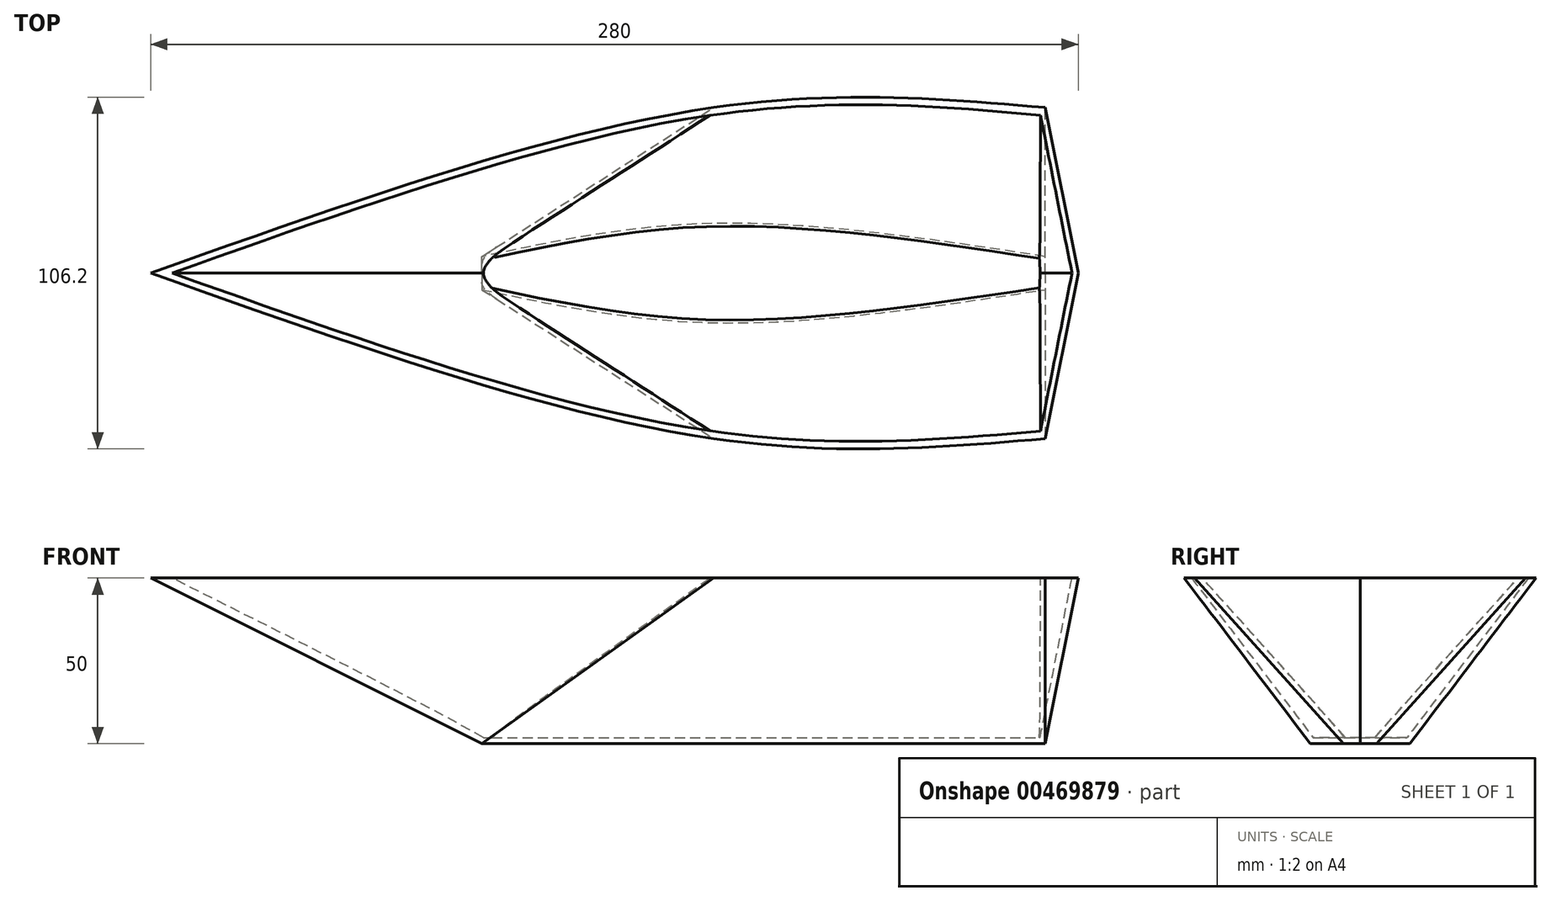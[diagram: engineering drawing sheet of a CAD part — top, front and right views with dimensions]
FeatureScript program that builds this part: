
annotation { "Feature Type Name" : "Feature", "Feature Type Description" : "" }
export const myFeature = defineFeature(function(context is Context, id is Id, definition is map)
    precondition{}
    {
        {
            var Q0;
            Q0=qCreatedBy(makeId("Top.planeOp"),FACE);
            var sketch = newSketch(context, id + "F0", { "sketchPlane" : qUnion([Q0])});
            skLineSegment(sketch, "E0", {"start": v(-100, 50) * mm, "end": v(-270, 50) * mm});
            skLineSegment(sketch, "E1", {"start": v(-100, -50) * mm, "end": v(-270, -50) * mm});
            skLineSegment(sketch, "E2", {"start": v(-270, 50) * mm, "end": v(-270, 0) * mm});
            skLineSegment(sketch, "E3", {"start": v(0, 50) * mm, "end": v(10, 0) * mm});
            skLineSegment(sketch, "E4", {"start": v(10, 0) * mm, "end": v(0, -50) * mm});
            skFitSpline(sketch, "E5", {"points": [v(-270, 0) * mm, v(-100, 50) * mm, v(0, 50) * mm], "startDerivative": vector(316.15, 112.56) * mm, "endDerivative": vector(219.26, -18.78) * mm});
            skFitSpline(sketch, "E6", {"points": [v(0, -50) * mm, v(-100, -50) * mm, v(-270, 0) * mm], "startDerivative": vector(-219.26, -18.78) * mm, "endDerivative": vector(-316.15, 112.56) * mm});
            skSolve(sketch);
        }
        {
            var Q0;
            Q0=qCreatedBy(makeId("Top.planeOp"),FACE);
            cPlane(context, id + "F1", {"entities" : qUnion([Q0]), "cplaneType" : CPlaneType.OFFSET, "offset" : 50 * mm, "oppositeDirection" : true, "width" : 150 * mm, "height" : 150 * mm});
        }
        {
            var Q0;
            Q0=qCreatedBy(id+"F1.planeOp",FACE);
            var sketch = newSketch(context, id + "F2", { "sketchPlane" : qUnion([Q0])});
            skLineSegment(sketch, "E7", {"start": v(0, 0) * mm, "end": v(5, 0) * mm});
            skLineSegment(sketch, "E8", {"start": v(0, 0) * mm, "end": v(0, -5) * mm});
            skLineSegment(sketch, "E9", {"start": v(0, 0) * mm, "end": v(0, 5) * mm});
            skLineSegment(sketch, "E10", {"start": v(-170, 0) * mm, "end": v(-170, -5) * mm});
            skLineSegment(sketch, "E11", {"start": v(-170, 0) * mm, "end": v(-170, 5) * mm});
            skFitSpline(sketch, "E12", {"points": [v(-170, -5) * mm, v(-100, -15) * mm, v(0, -5) * mm], "startDerivative": vector(146.51, -31.12) * mm, "endDerivative": vector(192.15, 29.35) * mm});
            skFitSpline(sketch, "E13", {"points": [v(0, 5) * mm, v(-100, 15) * mm, v(-170, 5) * mm], "startDerivative": vector(-192.15, 29.35) * mm, "endDerivative": vector(-146.51, -31.12) * mm});
            skSolve(sketch);
        }
        {
            var Q0;
            Q0=makeQuery(id+"F2.imprint","IMPRINT",FACE,{"disambiguationData":[TD([[makeQuery(id+"F2.imprint","IMPRINT",EDGE,{"derivedFrom":sQuery(id+"F2.wireOp",EDGE,"E8")}),-1.0]])]});
            var Q1;
            {var subQ2=sQuery(id+"F0.wireOp",EDGE,"E3");Q1=makeQuery(id+"F0.imprint","IMPRINT",FACE,{"disambiguationData":[TD([[makeQuery(id+"F0.imprint","IMPRINT",EDGE,{"derivedFrom":subQ2}),-1.0]])]});}
            loft(context, id + "F3", {"sheetProfilesArray" : [{ "sheetProfileEntities" : qUnion([Q0]) }, { "sheetProfileEntities" : qUnion([Q1]) }]});
        }
        {
            var Q0;
            {var subQ2=sQuery(id+"F0.wireOp",EDGE,"E3");Q0=makeQuery(id+"F3.opLoft","CAP_FACE",FACE,{"disambiguationData":[OSD([makeQuery(id+"F0.imprint","IMPRINT",FACE,{"disambiguationData":[TD([[makeQuery(id+"F0.imprint","IMPRINT",EDGE,{"derivedFrom":subQ2}),-1.0]])]})])],"isStart":true});}
            shell(context, id + "F4", {"entities" : qUnion([Q0]), "thickness" : 1.8 * mm});
        }
    });
